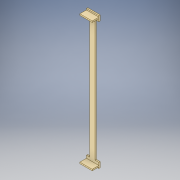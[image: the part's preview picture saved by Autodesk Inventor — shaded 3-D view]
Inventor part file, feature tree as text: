
AUTODESK INVENTOR PART (.ipt)
format: ipt  version: 2019 (Build 230136000, 136)  size: 404,992 bytes
history: native  units: mm
features: extrude x5, sketch x5, projected_geometry x3, fillet x2
ambient origin geometry x8: Origin, YZ Plane, XZ Plane, XY Plane, X Axis, Y Axis, Z Axis, Center Point
bodies: Solid1 (feature_tree)
feature tree (15):
  extrude  "Extrusion1"  Depth=2.0mm TaperAngle=0.0deg
  extrude  "Extrusion5"  Depth=2.0mm
  extrude  "Extrusion6"  Depth=4.0mm
  fillet  "Fillet1"  Radius=7.0mm
  fillet  "Fillet2"  Radius=10.0mm
  extrude  "Extrusion7"  Depth=10.0mm
  extrude  "Extrusion8"  Depth=4.0mm
  sketch  "Sketch1"  dims[d0=200.0mm d1=2.0mm d2=0.0mm]
  sketch  "Sketch5"  dims[d15=2.0mm d16=2.0mm]
  projected_geometry  "Projected Loop4"
  sketch  "Sketch7"  dims[d17=10.0mm d18=0.0mm d19=4.0mm d20=7.0mm d21=0.0mm d22=10.0mm]
  projected_geometry  "Projected Loop6"
  sketch  "Sketch8"  dims[d23=4.0mm d24=10.0mm]
  projected_geometry  "Projected Loop7"
  sketch  "Sketch9"  dims[d25=4.0mm d26=4.0mm d27=10.0mm d28=0.0mm d29=20.0mm d30=0.0mm]
